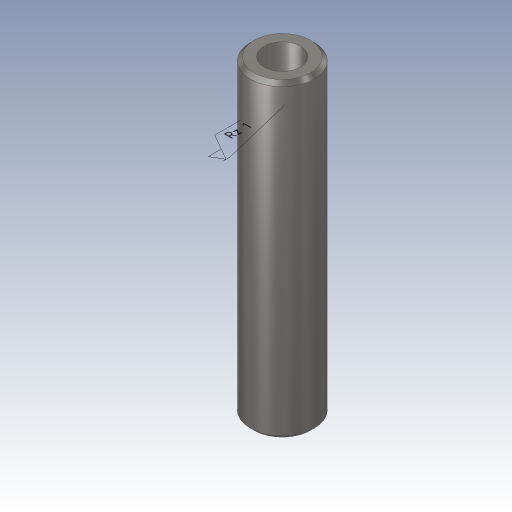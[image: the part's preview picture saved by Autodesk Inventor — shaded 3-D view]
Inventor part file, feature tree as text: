
AUTODESK INVENTOR PART (.ipt)
format: ipt  version: 2023.3 (Build 273359000, 359)  size: 149,504 bytes
history: native  units: in
note: dims shown in document units (in); Inventor stores cm internally (conversion verified against a paired STEP export)
features: other x2, extrude x1, chamfer x1, sketch x1
ambient origin geometry x8: Origin, YZ Plane, XZ Plane, XY Plane, X Axis, Y Axis, Z Axis, Center Point
bodies: Body1 (feature_tree)
feature tree (5):
  other  "Anmerkungen"
  extrude  "Extrusion3"  Depth=0.6693in
  chamfer  "Fase1"  Distance=0.6693in
  sketch  "Skizze3"  dims[d4=0.0787in d5=0.0295in d6=0.6693in d7=0.0in d8=0.0079in d9=0.0787in d10=45.0deg d11=0.3689in d12=0.1044in]
  other  "Oberflächenbeschaffenheit 1"
